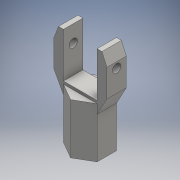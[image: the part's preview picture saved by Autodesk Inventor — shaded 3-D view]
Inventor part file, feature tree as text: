
AUTODESK INVENTOR PART (.ipt)
format: ipt  version: 2016 (Build 200138000, 138)  size: 165,376 bytes
history: native  units: mm
features: extrude x7, sketch x7
ambient origin geometry x8: Origin, YZ Plane, XZ Plane, XY Plane, X Axis, Y Axis, Z Axis, Center Point
bodies: Solid1 (feature_tree)
feature tree (14):
  extrude  "Extrusion1"  Depth=18.0mm TaperAngle=0.0deg
  extrude  "Extrusion2"  Depth=14.0mm TaperAngle=0.0deg
  extrude  "Extrusion3"  Depth=3.5mm
  extrude  "Extrusion4"  Depth=6.928203mm
  extrude  "Extrusion5"  Depth=6.928203mm TaperAngle=0.0deg
  extrude  "Extrusion6"  Depth=6.928203mm TaperAngle=0.0deg
  extrude  "Extrusion7"  Depth=10.0mm
  sketch  "Sketch1"  dims[d1=12.0mm d3=18.0mm d4=0.0mm]
  sketch  "Sketch2"  dims[d5=6.2mm d6=14.0mm d7=0.0mm]
  sketch  "Sketch3"  dims[d8=17.0mm d9=0.0mm d10=3.5mm]
  sketch  "Sketch4"  dims[d11=3.5mm d12=6.928203mm]
  sketch  "Sketch5"  dims[d13=6.928203mm d14=0.0mm d15=6.928203mm d16=0.0mm]
  sketch  "Sketch6"  dims[d18=3.0mm d19=6.928203mm d20=0.0mm]
  sketch  "Sketch7"  dims[d21=12.042772mm d23=1.727388mm d24=1.727388mm d25=10.0mm d26=0.0mm]
